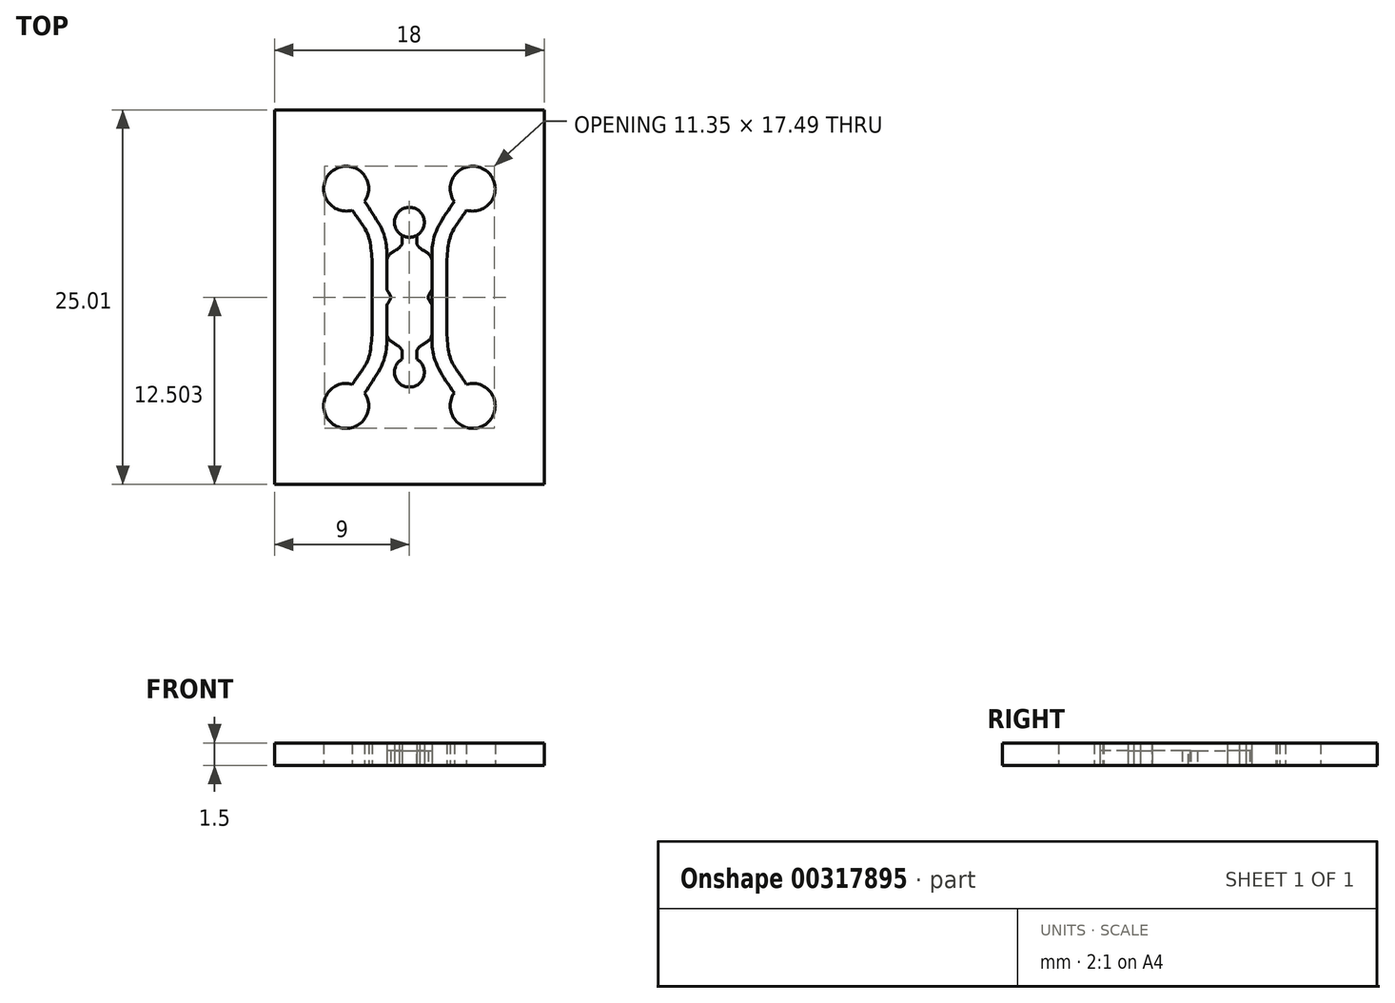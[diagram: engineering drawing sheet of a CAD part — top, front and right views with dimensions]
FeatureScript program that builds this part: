
annotation { "Feature Type Name" : "Feature", "Feature Type Description" : "" }
export const myFeature = defineFeature(function(context is Context, id is Id, definition is map)
    precondition{}
    {
        {
            var Q0;
            Q0=qCreatedBy(makeId("Top.planeOp"),FACE);
            var sketch = newSketch(context, id + "F0", { "sketchPlane" : qUnion([Q0])});
            skPoint(sketch, "E0.1.0.27", {"position": v(-35.15, 26.8) * mm});
            skCircle(sketch, "E1", {"center": v(0, 13.86) * mm, "radius": 50 * mm});
            skLineSegment(sketch, "E2", {"start": v(-12.54, -30.64) * mm, "end": v(-12.54, -12.64) * mm});
            skLineSegment(sketch, "E3", {"start": v(0, 13.86) * mm, "end": v(-50, 13.86) * mm});
            skLineSegment(sketch, "E4", {"start": v(-12.54, -12.64) * mm, "end": v(12.46, -12.64) * mm});
            skLineSegment(sketch, "E5", {"start": v(-12.54, -30.64) * mm, "end": v(12.46, -30.64) * mm});
            skLineSegment(sketch, "E6", {"start": v(12.46, -30.64) * mm, "end": v(12.46, -12.64) * mm});
            skLineSegment(sketch, "E7.left", {"start": v(-27.05, 0.86) * mm, "end": v(-27.05, -1.64) * mm});
            skLineSegment(sketch, "E8", {"start": v(-28.07, -3.26) * mm, "end": v(-28.07, -2.89) * mm});
            skFitSpline(sketch, "E9", {"points": [v(-28.07, -2.89) * mm, v(-28.05, -2.69) * mm, v(-27.87, -2.44) * mm], "startDerivative": vector(0, 0.47) * mm, "endDerivative": vector(0.58, 0.57) * mm});
            skFitSpline(sketch, "E10", {"points": [v(-27.87, -2.44) * mm, v(-27.6, -2.26) * mm, v(-27.23, -2) * mm, v(-27.05, -1.64) * mm], "startDerivative": vector(0.53, 0.49) * mm, "endDerivative": vector(0.1, 0.95) * mm});
            skLineSegment(sketch, "E11", {"start": v(-26.05, 0.86) * mm, "end": v(-26.05, -1.66) * mm});
            skPoint(sketch, "E12.third.point", {"position": v(-24.15, -7.57) * mm});
            skFitSpline(sketch, "E13", {"points": [v(-27.05, -1.64) * mm, v(-27.05, -2.14) * mm, v(-26.8, -3.43) * mm, v(-25.56, -5.53) * mm], "startDerivative": vector(-0.07, -2.14) * mm, "endDerivative": vector(3.18, -4.62) * mm});
            skPoint(sketch, "E14.third.point", {"position": v(-23.83, -5.88) * mm});
            skPoint(sketch, "E15.third.point", {"position": v(-22.85, -6.64) * mm});
            skArc(sketch, "E16", {"start": v(-28.55, -5.14) * mm, "mid": v(-27.58, -4.39) * mm, "end": v(-28.07, -3.26) * mm});
            skArc(sketch, "E17", {"start": v(-25.56, -5.53) * mm, "mid": v(-23.46, -7.6) * mm, "end": v(-24.74, -4.95) * mm});
            skFitSpline(sketch, "E18.MirrorCS", {"points": [v(-29.03, -2.89) * mm, v(-29.05, -2.69) * mm, v(-29.23, -2.44) * mm], "startDerivative": vector(0, 0.47) * mm, "endDerivative": vector(-0.58, 0.57) * mm});
            skLineSegment(sketch, "E19.MirrorCS", {"start": v(-29.03, -3.26) * mm, "end": v(-29.03, -2.89) * mm});
            skFitSpline(sketch, "E20.MirrorCS", {"points": [v(-29.23, -2.44) * mm, v(-29.5, -2.26) * mm, v(-29.87, -2) * mm, v(-30.05, -1.64) * mm], "startDerivative": vector(-0.53, 0.49) * mm, "endDerivative": vector(-0.1, 0.95) * mm});
            skPoint(sketch, "E21.MirrorP", {"position": v(-33.27, -5.88) * mm});
            skPoint(sketch, "E22.MirrorP", {"position": v(-32.95, -7.57) * mm});
            skArc(sketch, "E23.MirrorCS", {"start": v(-28.55, -5.14) * mm, "mid": v(-29.52, -4.39) * mm, "end": v(-29.03, -3.26) * mm});
            skArc(sketch, "E24.MirrorCS", {"start": v(-31.54, -5.53) * mm, "mid": v(-33.64, -7.6) * mm, "end": v(-32.36, -4.95) * mm});
            skLineSegment(sketch, "E25.MirrorCS", {"start": v(-30.05, 0.86) * mm, "end": v(-30.05, -1.64) * mm});
            skLineSegment(sketch, "E26.MirrorCS", {"start": v(-31.05, 0.86) * mm, "end": v(-31.05, -1.66) * mm});
            skFitSpline(sketch, "E27.MirrorCS", {"points": [v(-30.05, -1.64) * mm, v(-30.05, -2.14) * mm, v(-30.3, -3.43) * mm, v(-31.54, -5.53) * mm], "startDerivative": vector(0.07, -2.14) * mm, "endDerivative": vector(-3.18, -4.62) * mm});
            skPoint(sketch, "E28.MirrorP", {"position": v(-34.25, -6.64) * mm});
            skFitSpline(sketch, "E29", {"points": [v(-26.05, -1.66) * mm, v(-25.8, -3.26) * mm, v(-25.24, -4.22) * mm, v(-24.74, -4.95) * mm], "startDerivative": vector(0.34, -4.39) * mm, "endDerivative": vector(1.65, -2.5) * mm});
            skFitSpline(sketch, "E30.MirrorCS", {"points": [v(-31.05, -1.66) * mm, v(-31.3, -3.26) * mm, v(-31.86, -4.22) * mm, v(-32.36, -4.95) * mm], "startDerivative": vector(-0.34, -4.39) * mm, "endDerivative": vector(-1.65, -2.5) * mm});
            skCircle(sketch, "E31", {"center": v(-28.55, -4.14) * mm, "radius": 1 * mm});
            skFitSpline(sketch, "E32.MirrorCS", {"points": [v(-28.07, 4.61) * mm, v(-28.05, 4.41) * mm, v(-27.87, 4.17) * mm], "startDerivative": vector(0, -0.47) * mm, "endDerivative": vector(0.58, -0.57) * mm});
            skFitSpline(sketch, "E33.MirrorCS", {"points": [v(-29.03, 4.61) * mm, v(-29.05, 4.41) * mm, v(-29.23, 4.17) * mm], "startDerivative": vector(0, -0.47) * mm, "endDerivative": vector(-0.58, -0.57) * mm});
            skFitSpline(sketch, "E34.MirrorCS", {"points": [v(-27.87, 4.17) * mm, v(-27.6, 3.98) * mm, v(-27.23, 3.72) * mm, v(-27.05, 3.36) * mm], "startDerivative": vector(0.53, -0.49) * mm, "endDerivative": vector(0.1, -0.95) * mm});
            skFitSpline(sketch, "E35.MirrorCS", {"points": [v(-29.23, 4.17) * mm, v(-29.5, 3.98) * mm, v(-29.87, 3.72) * mm, v(-30.05, 3.36) * mm], "startDerivative": vector(-0.53, -0.49) * mm, "endDerivative": vector(-0.1, -0.95) * mm});
            skLineSegment(sketch, "E36.MirrorCS", {"start": v(-28.07, 4.99) * mm, "end": v(-28.07, 4.61) * mm});
            skLineSegment(sketch, "E37.MirrorCS", {"start": v(-29.03, 4.99) * mm, "end": v(-29.03, 4.61) * mm});
            skArc(sketch, "E38.MirrorCS", {"start": v(-28.55, 6.86) * mm, "mid": v(-27.58, 6.11) * mm, "end": v(-28.07, 4.99) * mm});
            skPoint(sketch, "E39.MirrorP", {"position": v(-32.95, 9.3) * mm});
            skFitSpline(sketch, "E40.MirrorCS", {"points": [v(-31.05, 3.4) * mm, v(-31.3, 4.99) * mm, v(-31.86, 5.94) * mm, v(-32.36, 6.67) * mm], "startDerivative": vector(-0.34, 4.39) * mm, "endDerivative": vector(-1.65, 2.5) * mm});
            skLineSegment(sketch, "E41.MirrorCS", {"start": v(-26.05, 0.86) * mm, "end": v(-26.05, 3.4) * mm});
            skLineSegment(sketch, "E42.MirrorCS", {"start": v(-27.05, 0.86) * mm, "end": v(-27.05, 3.36) * mm});
            skPoint(sketch, "E43.MirrorP", {"position": v(-22.85, 8.36) * mm});
            skFitSpline(sketch, "E44.MirrorCS", {"points": [v(-30.05, 3.36) * mm, v(-30.05, 3.86) * mm, v(-30.3, 5.15) * mm, v(-31.54, 7.25) * mm], "startDerivative": vector(0.07, 2.14) * mm, "endDerivative": vector(-3.18, 4.62) * mm});
            skPoint(sketch, "E45.MirrorP", {"position": v(-24.15, 9.3) * mm});
            skLineSegment(sketch, "E46.MirrorCS", {"start": v(-31.05, 0.86) * mm, "end": v(-31.05, 3.4) * mm});
            skLineSegment(sketch, "E47.MirrorCS", {"start": v(-30.05, 0.86) * mm, "end": v(-30.05, 3.36) * mm});
            skFitSpline(sketch, "E48.MirrorCS", {"points": [v(-27.05, 3.36) * mm, v(-27.05, 3.86) * mm, v(-26.8, 5.15) * mm, v(-25.56, 7.25) * mm], "startDerivative": vector(-0.07, 2.14) * mm, "endDerivative": vector(3.18, 4.62) * mm});
            skCircle(sketch, "E49.MirrorC", {"center": v(-28.55, 5.86) * mm, "radius": 1 * mm});
            skPoint(sketch, "E50.MirrorP", {"position": v(-34.25, 8.36) * mm});
            skFitSpline(sketch, "E51.MirrorCS", {"points": [v(-26.05, 3.4) * mm, v(-25.8, 4.99) * mm, v(-25.24, 5.94) * mm, v(-24.74, 6.67) * mm], "startDerivative": vector(0.34, 4.39) * mm, "endDerivative": vector(1.65, 2.5) * mm});
            skArc(sketch, "E52.MirrorCS", {"start": v(-28.55, 6.86) * mm, "mid": v(-29.52, 6.11) * mm, "end": v(-29.03, 4.99) * mm});
            skArc(sketch, "E53.MirrorCS", {"start": v(-25.56, 7.25) * mm, "mid": v(-23.46, 9.34) * mm, "end": v(-24.74, 6.67) * mm});
            skPoint(sketch, "E54.MirrorP", {"position": v(-23.83, 7.6) * mm});
            skArc(sketch, "E55.MirrorCS", {"start": v(-31.54, 7.25) * mm, "mid": v(-33.64, 9.34) * mm, "end": v(-32.36, 6.67) * mm});
            skPoint(sketch, "E56.MirrorP", {"position": v(-33.27, 7.6) * mm});
            skFitSpline(sketch, "E57", {"points": [v(-29.8, 0.86) * mm, v(-29.81, 0.79) * mm, v(-30.05, 0.36) * mm], "startDerivative": vector(0, -0.22) * mm, "endDerivative": vector(-0.44, -0.71) * mm});
            skArc(sketch, "E58", {"start": v(-29.81, 0.79) * mm, "mid": v(-29.8, 0.83) * mm, "end": v(-29.8, 0.86) * mm});
            skFitSpline(sketch, "E59.MirrorCS", {"points": [v(-29.8, 0.86) * mm, v(-29.81, 0.94) * mm, v(-30.05, 1.36) * mm], "startDerivative": vector(0, 0.22) * mm, "endDerivative": vector(-0.44, 0.71) * mm});
            skArc(sketch, "E60.MirrorCS", {"start": v(-29.81, 0.94) * mm, "mid": v(-29.8, 0.9) * mm, "end": v(-29.8, 0.86) * mm});
            skArc(sketch, "E61.MirrorCS", {"start": v(-27.29, 0.79) * mm, "mid": v(-27.3, 0.83) * mm, "end": v(-27.3, 0.86) * mm});
            skArc(sketch, "E62.MirrorCS", {"start": v(-27.29, 0.94) * mm, "mid": v(-27.3, 0.9) * mm, "end": v(-27.3, 0.86) * mm});
            skFitSpline(sketch, "E63.MirrorCS", {"points": [v(-27.3, 0.86) * mm, v(-27.29, 0.79) * mm, v(-27.05, 0.36) * mm], "startDerivative": vector(0, -0.22) * mm, "endDerivative": vector(0.44, -0.71) * mm});
            skFitSpline(sketch, "E64.MirrorCS", {"points": [v(-27.3, 0.86) * mm, v(-27.29, 0.94) * mm, v(-27.05, 1.36) * mm], "startDerivative": vector(0, 0.22) * mm, "endDerivative": vector(0.44, 0.71) * mm});
            skCircle(sketch, "E65.MirrorC", {"center": v(0, 11.64) * mm, "radius": 1 * mm});
            skLineSegment(sketch, "E66.right", {"start": v(-37.55, -11.64) * mm, "end": v(-37.55, 13.37) * mm});
            skLineSegment(sketch, "E67.bottom", {"start": v(-19.55, 13.37) * mm, "end": v(-37.55, 13.37) * mm});
            skLineSegment(sketch, "E67.top", {"start": v(-19.55, -11.64) * mm, "end": v(-37.55, -11.64) * mm});
            skLineSegment(sketch, "E67.left", {"start": v(-19.55, 13.37) * mm, "end": v(-19.55, -11.64) * mm});
            skLineSegment(sketch, "E67.right", {"start": v(-37.55, 13.37) * mm, "end": v(-37.55, -11.64) * mm});
            skArc(sketch, "E68.MirrorCS", {"start": v(-0.06, -22.85) * mm, "mid": v(-0.02, -22.84) * mm, "end": v(0.01, -22.83) * mm});
            skFitSpline(sketch, "E69.MirrorCS", {"points": [v(0.01, -22.83) * mm, v(-0.06, -22.85) * mm, v(-0.49, -23.08) * mm], "startDerivative": vector(-0.22, 0) * mm, "endDerivative": vector(-0.71, -0.44) * mm});
            skArc(sketch, "E70.MirrorCS", {"start": v(0.09, -22.85) * mm, "mid": v(0.05, -22.84) * mm, "end": v(0.01, -22.83) * mm});
            skFitSpline(sketch, "E71.MirrorCS", {"points": [v(0.01, -22.83) * mm, v(0.09, -22.85) * mm, v(0.51, -23.08) * mm], "startDerivative": vector(0.22, 0) * mm, "endDerivative": vector(0.71, -0.44) * mm});
            skArc(sketch, "E72.MirrorCS", {"start": v(-0.06, -20.32) * mm, "mid": v(-0.02, -20.33) * mm, "end": v(0.01, -20.33) * mm});
            skFitSpline(sketch, "E73.MirrorCS", {"points": [v(0.01, -20.33) * mm, v(0.09, -20.32) * mm, v(0.51, -20.08) * mm], "startDerivative": vector(0.22, 0) * mm, "endDerivative": vector(0.71, 0.44) * mm});
            skFitSpline(sketch, "E74.MirrorCS", {"points": [v(0.01, -20.33) * mm, v(-0.06, -20.32) * mm, v(-0.49, -20.08) * mm], "startDerivative": vector(-0.22, 0) * mm, "endDerivative": vector(-0.71, 0.44) * mm});
            skArc(sketch, "E75.MirrorCS", {"start": v(0.09, -20.32) * mm, "mid": v(0.05, -20.33) * mm, "end": v(0.01, -20.33) * mm});
            skFitSpline(sketch, "E76.MirrorCS", {"points": [v(3.32, -22.26) * mm, v(3.13, -22.53) * mm, v(2.87, -22.9) * mm, v(2.51, -23.08) * mm], "startDerivative": vector(-0.49, -0.53) * mm, "endDerivative": vector(-0.95, -0.1) * mm});
            skFitSpline(sketch, "E77.MirrorCS", {"points": [v(3.76, -22.07) * mm, v(3.56, -22.08) * mm, v(3.32, -22.26) * mm], "startDerivative": vector(-0.47, 0) * mm, "endDerivative": vector(-0.57, -0.58) * mm});
            skLineSegment(sketch, "E78.MirrorCS", {"start": v(4.14, -22.07) * mm, "end": v(3.76, -22.07) * mm});
            skFitSpline(sketch, "E79.MirrorCS", {"points": [v(3.32, -20.9) * mm, v(3.13, -20.63) * mm, v(2.87, -20.26) * mm, v(2.51, -20.08) * mm], "startDerivative": vector(-0.49, 0.53) * mm, "endDerivative": vector(-0.95, 0.1) * mm});
            skFitSpline(sketch, "E80.MirrorCS", {"points": [v(3.76, -21.1) * mm, v(3.56, -21.08) * mm, v(3.32, -20.9) * mm], "startDerivative": vector(-0.47, 0) * mm, "endDerivative": vector(-0.57, 0.58) * mm});
            skLineSegment(sketch, "E81.MirrorCS", {"start": v(4.14, -21.1) * mm, "end": v(3.76, -21.1) * mm});
            skFitSpline(sketch, "E82.MirrorCS", {"points": [v(-3.29, -22.26) * mm, v(-3.1, -22.53) * mm, v(-2.84, -22.9) * mm, v(-2.49, -23.08) * mm], "startDerivative": vector(0.49, -0.53) * mm, "endDerivative": vector(0.95, -0.1) * mm});
            skFitSpline(sketch, "E83.MirrorCS", {"points": [v(-3.29, -20.9) * mm, v(-3.1, -20.63) * mm, v(-2.84, -20.26) * mm, v(-2.49, -20.08) * mm], "startDerivative": vector(0.49, 0.53) * mm, "endDerivative": vector(0.95, 0.1) * mm});
            skLineSegment(sketch, "E84.MirrorCS", {"start": v(-4.11, -22.07) * mm, "end": v(-3.74, -22.07) * mm});
            skFitSpline(sketch, "E85.MirrorCS", {"points": [v(-3.74, -21.1) * mm, v(-3.54, -21.08) * mm, v(-3.29, -20.9) * mm], "startDerivative": vector(0.47, 0) * mm, "endDerivative": vector(0.57, 0.58) * mm});
            skFitSpline(sketch, "E86.MirrorCS", {"points": [v(-3.74, -22.07) * mm, v(-3.54, -22.08) * mm, v(-3.29, -22.26) * mm], "startDerivative": vector(0.47, 0) * mm, "endDerivative": vector(0.57, -0.58) * mm});
            skLineSegment(sketch, "E87.MirrorCS", {"start": v(-4.11, -21.1) * mm, "end": v(-3.74, -21.1) * mm});
            skLineSegment(sketch, "E88.MirrorCS", {"start": v(0.01, -23.08) * mm, "end": v(-2.49, -23.08) * mm});
            skLineSegment(sketch, "E89.MirrorCS", {"start": v(0.01, -20.08) * mm, "end": v(2.51, -20.08) * mm});
            skLineSegment(sketch, "E90.MirrorCS", {"start": v(0.01, -19.08) * mm, "end": v(-2.51, -19.08) * mm});
            skLineSegment(sketch, "E91.MirrorCS", {"start": v(0.01, -19.08) * mm, "end": v(2.54, -19.08) * mm});
            skFitSpline(sketch, "E92.MirrorCS", {"points": [v(2.54, -24.08) * mm, v(4.14, -24.34) * mm, v(5.1, -24.9) * mm, v(5.82, -25.4) * mm], "startDerivative": vector(4.39, -0.34) * mm, "endDerivative": vector(2.5, -1.65) * mm});
            skFitSpline(sketch, "E93.MirrorCS", {"points": [v(2.54, -19.08) * mm, v(4.14, -18.83) * mm, v(5.1, -18.27) * mm, v(5.82, -17.78) * mm], "startDerivative": vector(4.39, 0.34) * mm, "endDerivative": vector(2.5, 1.65) * mm});
            skLineSegment(sketch, "E94.MirrorCS", {"start": v(0.01, -20.08) * mm, "end": v(-2.49, -20.08) * mm});
            skFitSpline(sketch, "E95.MirrorCS", {"points": [v(-2.51, -24.08) * mm, v(-4.1, -24.34) * mm, v(-5.07, -24.9) * mm, v(-5.8, -25.4) * mm], "startDerivative": vector(-4.39, -0.34) * mm, "endDerivative": vector(-2.5, -1.65) * mm});
            skLineSegment(sketch, "E96.MirrorCS", {"start": v(0.01, -23.08) * mm, "end": v(2.51, -23.08) * mm});
            skLineSegment(sketch, "E97.MirrorCS", {"start": v(0.01, -24.08) * mm, "end": v(2.54, -24.08) * mm});
            skLineSegment(sketch, "E98.MirrorCS", {"start": v(0.01, -24.08) * mm, "end": v(-2.51, -24.08) * mm});
            skArc(sketch, "E99.MirrorCS", {"start": v(-5.99, -21.58) * mm, "mid": v(-5.24, -20.62) * mm, "end": v(-4.11, -21.1) * mm});
            skFitSpline(sketch, "E100.MirrorCS", {"points": [v(2.51, -23.08) * mm, v(3.01, -23.08) * mm, v(4.3, -23.33) * mm, v(6.4, -24.58) * mm], "startDerivative": vector(2.14, 0.07) * mm, "endDerivative": vector(4.62, -3.18) * mm});
            skFitSpline(sketch, "E101.MirrorCS", {"points": [v(-2.49, -20.08) * mm, v(-2.99, -20.08) * mm, v(-4.28, -19.84) * mm, v(-6.38, -18.59) * mm], "startDerivative": vector(-2.14, -0.07) * mm, "endDerivative": vector(-4.62, 3.18) * mm});
            skArc(sketch, "E102.MirrorCS", {"start": v(6.01, -21.58) * mm, "mid": v(5.26, -20.62) * mm, "end": v(4.14, -21.1) * mm});
            skCircle(sketch, "E103.MirrorC", {"center": v(-4.99, -21.58) * mm, "radius": 1 * mm});
            skFitSpline(sketch, "E104.MirrorCS", {"points": [v(-2.51, -19.08) * mm, v(-4.1, -18.83) * mm, v(-5.07, -18.27) * mm, v(-5.8, -17.78) * mm], "startDerivative": vector(-4.39, 0.34) * mm, "endDerivative": vector(-2.5, 1.65) * mm});
            skFitSpline(sketch, "E105.MirrorCS", {"points": [v(2.51, -20.08) * mm, v(3.01, -20.08) * mm, v(4.3, -19.84) * mm, v(6.4, -18.59) * mm], "startDerivative": vector(2.14, -0.07) * mm, "endDerivative": vector(4.62, 3.18) * mm});
            skCircle(sketch, "E106.MirrorC", {"center": v(5.01, -21.58) * mm, "radius": 1 * mm});
            skFitSpline(sketch, "E107.MirrorCS", {"points": [v(-2.49, -23.08) * mm, v(-2.99, -23.08) * mm, v(-4.28, -23.33) * mm, v(-6.38, -24.58) * mm], "startDerivative": vector(-2.14, 0.07) * mm, "endDerivative": vector(-4.62, -3.18) * mm});
            skPoint(sketch, "E108.MirrorP", {"position": v(7.51, -15.88) * mm});
            skPoint(sketch, "E109.MirrorP", {"position": v(8.44, -17.18) * mm});
            skArc(sketch, "E110.MirrorCS", {"start": v(6.4, -24.58) * mm, "mid": v(8.49, -26.68) * mm, "end": v(5.82, -25.4) * mm});
            skPoint(sketch, "E111.MirrorP", {"position": v(7.51, -27.28) * mm});
            skArc(sketch, "E112.MirrorCS", {"start": v(-6.38, -24.58) * mm, "mid": v(-8.46, -26.68) * mm, "end": v(-5.8, -25.4) * mm});
            skArc(sketch, "E113.MirrorCS", {"start": v(-5.99, -21.58) * mm, "mid": v(-5.24, -22.55) * mm, "end": v(-4.11, -22.07) * mm});
            skArc(sketch, "E114.MirrorCS", {"start": v(6.4, -18.59) * mm, "mid": v(8.49, -16.5) * mm, "end": v(5.82, -17.78) * mm});
            skArc(sketch, "E115.MirrorCS", {"start": v(6.01, -21.58) * mm, "mid": v(5.26, -22.55) * mm, "end": v(4.14, -22.07) * mm});
            skPoint(sketch, "E116.MirrorP", {"position": v(-7.49, -27.28) * mm});
            skPoint(sketch, "E117.MirrorP", {"position": v(-8.42, -17.18) * mm});
            skPoint(sketch, "E118.MirrorP", {"position": v(-6.73, -26.3) * mm});
            skPoint(sketch, "E119.MirrorP", {"position": v(6.76, -26.3) * mm});
            skPoint(sketch, "E120.MirrorP", {"position": v(-7.49, -15.88) * mm});
            skPoint(sketch, "E121.MirrorP", {"position": v(-6.73, -16.86) * mm});
            skPoint(sketch, "E122.MirrorP", {"position": v(-8.42, -25.99) * mm});
            skPoint(sketch, "E123.MirrorP", {"position": v(8.44, -25.99) * mm});
            skArc(sketch, "E124.MirrorCS", {"start": v(-6.38, -18.59) * mm, "mid": v(-8.46, -16.5) * mm, "end": v(-5.8, -17.78) * mm});
            skPoint(sketch, "E125.MirrorP", {"position": v(6.76, -16.86) * mm});
            skFitSpline(sketch, "E126.MirrorCS", {"points": [v(0.01, -20.33) * mm, v(0.09, -20.32) * mm, v(0.51, -20.08) * mm], "startDerivative": vector(0.22, 0) * mm, "endDerivative": vector(0.71, 0.44) * mm});
            skFitSpline(sketch, "E127.MirrorCS", {"points": [v(0.01, -20.33) * mm, v(-0.06, -20.32) * mm, v(-0.49, -20.08) * mm], "startDerivative": vector(-0.22, 0) * mm, "endDerivative": vector(-0.71, 0.44) * mm});
            skFitSpline(sketch, "E128.MirrorCS", {"points": [v(0.01, -22.83) * mm, v(0.09, -22.85) * mm, v(0.51, -23.08) * mm], "startDerivative": vector(0.22, 0) * mm, "endDerivative": vector(0.71, -0.44) * mm});
            skFitSpline(sketch, "E129.MirrorCS", {"points": [v(0.01, -22.83) * mm, v(-0.06, -22.85) * mm, v(-0.49, -23.08) * mm], "startDerivative": vector(-0.22, 0) * mm, "endDerivative": vector(-0.71, -0.44) * mm});
            skFitSpline(sketch, "E130.MirrorCS", {"points": [v(-3.29, -22.26) * mm, v(-3.1, -22.53) * mm, v(-2.84, -22.9) * mm, v(-2.49, -23.08) * mm], "startDerivative": vector(0.49, -0.53) * mm, "endDerivative": vector(0.95, -0.1) * mm});
            skFitSpline(sketch, "E131.MirrorCS", {"points": [v(-3.29, -20.9) * mm, v(-3.1, -20.63) * mm, v(-2.84, -20.26) * mm, v(-2.49, -20.08) * mm], "startDerivative": vector(0.49, 0.53) * mm, "endDerivative": vector(0.95, 0.1) * mm});
            skFitSpline(sketch, "E132.MirrorCS", {"points": [v(3.32, -20.9) * mm, v(3.13, -20.63) * mm, v(2.87, -20.26) * mm, v(2.51, -20.08) * mm], "startDerivative": vector(-0.49, 0.53) * mm, "endDerivative": vector(-0.95, 0.1) * mm});
            skFitSpline(sketch, "E133.MirrorCS", {"points": [v(-3.74, -21.1) * mm, v(-3.54, -21.08) * mm, v(-3.29, -20.9) * mm], "startDerivative": vector(0.47, 0) * mm, "endDerivative": vector(0.57, 0.58) * mm});
            skFitSpline(sketch, "E134.MirrorCS", {"points": [v(3.32, -22.26) * mm, v(3.13, -22.53) * mm, v(2.87, -22.9) * mm, v(2.51, -23.08) * mm], "startDerivative": vector(-0.49, -0.53) * mm, "endDerivative": vector(-0.95, -0.1) * mm});
            skFitSpline(sketch, "E135.MirrorCS", {"points": [v(3.76, -21.1) * mm, v(3.56, -21.08) * mm, v(3.32, -20.9) * mm], "startDerivative": vector(-0.47, 0) * mm, "endDerivative": vector(-0.57, 0.58) * mm});
            skFitSpline(sketch, "E136.MirrorCS", {"points": [v(-2.51, -19.08) * mm, v(-4.1, -18.83) * mm, v(-5.07, -18.27) * mm, v(-5.8, -17.78) * mm], "startDerivative": vector(-4.39, 0.34) * mm, "endDerivative": vector(-2.5, 1.65) * mm});
            skFitSpline(sketch, "E137.MirrorCS", {"points": [v(-2.51, -24.08) * mm, v(-4.1, -24.34) * mm, v(-5.07, -24.9) * mm, v(-5.8, -25.4) * mm], "startDerivative": vector(-4.39, -0.34) * mm, "endDerivative": vector(-2.5, -1.65) * mm});
            skFitSpline(sketch, "E138.MirrorCS", {"points": [v(-2.49, -23.08) * mm, v(-2.99, -23.08) * mm, v(-4.28, -23.33) * mm, v(-6.38, -24.58) * mm], "startDerivative": vector(-2.14, 0.07) * mm, "endDerivative": vector(-4.62, -3.18) * mm});
            skFitSpline(sketch, "E139.MirrorCS", {"points": [v(-2.49, -20.08) * mm, v(-2.99, -20.08) * mm, v(-4.28, -19.84) * mm, v(-6.38, -18.59) * mm], "startDerivative": vector(-2.14, -0.07) * mm, "endDerivative": vector(-4.62, 3.18) * mm});
            skArc(sketch, "E140.MirrorCS", {"start": v(-0.06, 48.05) * mm, "mid": v(-0.02, 48.06) * mm, "end": v(0.01, 48.06) * mm});
            skArc(sketch, "E141.MirrorCS", {"start": v(0.09, 48.05) * mm, "mid": v(0.05, 48.06) * mm, "end": v(0.01, 48.06) * mm});
            skLineSegment(sketch, "E142.MirrorCS", {"start": v(0.01, 46.81) * mm, "end": v(-2.51, 46.81) * mm});
            skLineSegment(sketch, "E143.MirrorCS", {"start": v(0.01, 47.81) * mm, "end": v(-2.49, 47.81) * mm});
            skFitSpline(sketch, "E144.MirrorCS", {"points": [v(0.01, 48.06) * mm, v(0.09, 48.05) * mm, v(0.51, 47.81) * mm], "startDerivative": vector(0.22, 0) * mm, "endDerivative": vector(0.71, -0.44) * mm});
            skFitSpline(sketch, "E145.MirrorCS", {"points": [v(0.01, 48.06) * mm, v(-0.06, 48.05) * mm, v(-0.49, 47.81) * mm], "startDerivative": vector(-0.22, 0) * mm, "endDerivative": vector(-0.71, -0.44) * mm});
            skFitSpline(sketch, "E146.MirrorCS", {"points": [v(0.01, 48.06) * mm, v(-0.06, 48.05) * mm, v(-0.49, 47.81) * mm], "startDerivative": vector(-0.22, 0) * mm, "endDerivative": vector(-0.71, -0.44) * mm});
            skFitSpline(sketch, "E147.MirrorCS", {"points": [v(0.01, 48.06) * mm, v(0.09, 48.05) * mm, v(0.51, 47.81) * mm], "startDerivative": vector(0.22, 0) * mm, "endDerivative": vector(0.71, -0.44) * mm});
            skArc(sketch, "E148.MirrorCS", {"start": v(-0.06, 50.57) * mm, "mid": v(-0.02, 50.57) * mm, "end": v(0.01, 50.56) * mm});
            skArc(sketch, "E149.MirrorCS", {"start": v(0.09, 50.57) * mm, "mid": v(0.05, 50.57) * mm, "end": v(0.01, 50.56) * mm});
            skFitSpline(sketch, "E150.MirrorCS", {"points": [v(0.01, 50.56) * mm, v(0.09, 50.57) * mm, v(0.51, 50.81) * mm], "startDerivative": vector(0.22, 0) * mm, "endDerivative": vector(0.71, 0.44) * mm});
            skLineSegment(sketch, "E151.MirrorCS", {"start": v(0.01, 50.81) * mm, "end": v(-2.49, 50.81) * mm});
            skFitSpline(sketch, "E152.MirrorCS", {"points": [v(0.01, 50.56) * mm, v(-0.06, 50.57) * mm, v(-0.49, 50.81) * mm], "startDerivative": vector(-0.22, 0) * mm, "endDerivative": vector(-0.71, 0.44) * mm});
            skLineSegment(sketch, "E153.MirrorCS", {"start": v(0.01, 51.81) * mm, "end": v(-2.51, 51.81) * mm});
            skFitSpline(sketch, "E154.MirrorCS", {"points": [v(0.01, 50.56) * mm, v(0.09, 50.57) * mm, v(0.51, 50.81) * mm], "startDerivative": vector(0.22, 0) * mm, "endDerivative": vector(0.71, 0.44) * mm});
            skFitSpline(sketch, "E155.MirrorCS", {"points": [v(0.01, 50.56) * mm, v(-0.06, 50.57) * mm, v(-0.49, 50.81) * mm], "startDerivative": vector(-0.22, 0) * mm, "endDerivative": vector(-0.71, 0.44) * mm});
            skLineSegment(sketch, "E156.MirrorCS", {"start": v(-4.11, 49.8) * mm, "end": v(-3.74, 49.8) * mm});
            skFitSpline(sketch, "E157.MirrorCS", {"points": [v(-3.29, 48.63) * mm, v(-3.1, 48.36) * mm, v(-2.84, 48) * mm, v(-2.49, 47.81) * mm], "startDerivative": vector(0.49, -0.53) * mm, "endDerivative": vector(0.95, -0.1) * mm});
            skLineSegment(sketch, "E158.MirrorCS", {"start": v(-4.11, 48.83) * mm, "end": v(-3.74, 48.83) * mm});
            skFitSpline(sketch, "E159.MirrorCS", {"points": [v(-3.74, 48.83) * mm, v(-3.54, 48.81) * mm, v(-3.29, 48.63) * mm], "startDerivative": vector(0.47, 0) * mm, "endDerivative": vector(0.57, -0.58) * mm});
            skLineSegment(sketch, "E160.MirrorCS", {"start": v(0.01, 47.81) * mm, "end": v(2.51, 47.81) * mm});
            skFitSpline(sketch, "E161.MirrorCS", {"points": [v(-3.29, 50) * mm, v(-3.1, 50.26) * mm, v(-2.84, 50.63) * mm, v(-2.49, 50.81) * mm], "startDerivative": vector(0.49, 0.53) * mm, "endDerivative": vector(0.95, 0.1) * mm});
            skFitSpline(sketch, "E162.MirrorCS", {"points": [v(3.76, 49.8) * mm, v(3.56, 49.81) * mm, v(3.32, 50) * mm], "startDerivative": vector(-0.47, 0) * mm, "endDerivative": vector(-0.57, 0.58) * mm});
            skFitSpline(sketch, "E163.MirrorCS", {"points": [v(-3.74, 49.8) * mm, v(-3.54, 49.81) * mm, v(-3.29, 50) * mm], "startDerivative": vector(0.47, 0) * mm, "endDerivative": vector(0.57, 0.58) * mm});
            skFitSpline(sketch, "E164.MirrorCS", {"points": [v(-3.74, 48.83) * mm, v(-3.54, 48.81) * mm, v(-3.29, 48.63) * mm], "startDerivative": vector(0.47, 0) * mm, "endDerivative": vector(0.57, -0.58) * mm});
            skLineSegment(sketch, "E165.MirrorCS", {"start": v(4.14, 49.8) * mm, "end": v(3.76, 49.8) * mm});
            skFitSpline(sketch, "E166.MirrorCS", {"points": [v(3.32, 48.63) * mm, v(3.13, 48.36) * mm, v(2.87, 48) * mm, v(2.51, 47.81) * mm], "startDerivative": vector(-0.49, -0.53) * mm, "endDerivative": vector(-0.95, -0.1) * mm});
            skFitSpline(sketch, "E167.MirrorCS", {"points": [v(3.32, 50) * mm, v(3.13, 50.26) * mm, v(2.87, 50.63) * mm, v(2.51, 50.81) * mm], "startDerivative": vector(-0.49, 0.53) * mm, "endDerivative": vector(-0.95, 0.1) * mm});
            skFitSpline(sketch, "E168.MirrorCS", {"points": [v(-3.29, 48.63) * mm, v(-3.1, 48.36) * mm, v(-2.84, 48) * mm, v(-2.49, 47.81) * mm], "startDerivative": vector(0.49, -0.53) * mm, "endDerivative": vector(0.95, -0.1) * mm});
            skFitSpline(sketch, "E169.MirrorCS", {"points": [v(-3.29, 50) * mm, v(-3.1, 50.26) * mm, v(-2.84, 50.63) * mm, v(-2.49, 50.81) * mm], "startDerivative": vector(0.49, 0.53) * mm, "endDerivative": vector(0.95, 0.1) * mm});
            skFitSpline(sketch, "E170.MirrorCS", {"points": [v(-3.74, 49.8) * mm, v(-3.54, 49.81) * mm, v(-3.29, 50) * mm], "startDerivative": vector(0.47, 0) * mm, "endDerivative": vector(0.57, 0.58) * mm});
            skLineSegment(sketch, "E171.MirrorCS", {"start": v(4.14, 48.83) * mm, "end": v(3.76, 48.83) * mm});
            skLineSegment(sketch, "E172.MirrorCS", {"start": v(0.01, 46.81) * mm, "end": v(2.54, 46.81) * mm});
            skFitSpline(sketch, "E173.MirrorCS", {"points": [v(3.76, 48.83) * mm, v(3.56, 48.81) * mm, v(3.32, 48.63) * mm], "startDerivative": vector(-0.47, 0) * mm, "endDerivative": vector(-0.57, -0.58) * mm});
            skFitSpline(sketch, "E174.MirrorCS", {"points": [v(3.32, 50) * mm, v(3.13, 50.26) * mm, v(2.87, 50.63) * mm, v(2.51, 50.81) * mm], "startDerivative": vector(-0.49, 0.53) * mm, "endDerivative": vector(-0.95, 0.1) * mm});
            skFitSpline(sketch, "E175.MirrorCS", {"points": [v(3.32, 48.63) * mm, v(3.13, 48.36) * mm, v(2.87, 48) * mm, v(2.51, 47.81) * mm], "startDerivative": vector(-0.49, -0.53) * mm, "endDerivative": vector(-0.95, -0.1) * mm});
            skFitSpline(sketch, "E176.MirrorCS", {"points": [v(3.76, 48.83) * mm, v(3.56, 48.81) * mm, v(3.32, 48.63) * mm], "startDerivative": vector(-0.47, 0) * mm, "endDerivative": vector(-0.57, -0.58) * mm});
            skLineSegment(sketch, "E177.MirrorCS", {"start": v(0.01, 50.81) * mm, "end": v(2.51, 50.81) * mm});
            skLineSegment(sketch, "E178.MirrorCS", {"start": v(0.01, 51.81) * mm, "end": v(2.54, 51.81) * mm});
            skArc(sketch, "E179.MirrorCS", {"start": v(-5.99, 49.31) * mm, "mid": v(-5.24, 48.35) * mm, "end": v(-4.11, 48.83) * mm});
            skArc(sketch, "E180.MirrorCS", {"start": v(6.01, 49.31) * mm, "mid": v(5.26, 48.35) * mm, "end": v(4.14, 48.83) * mm});
            skCircle(sketch, "E181.MirrorC", {"center": v(5.01, 49.31) * mm, "radius": 1 * mm});
            skCircle(sketch, "E182.MirrorC", {"center": v(-4.99, 49.31) * mm, "radius": 1 * mm});
            skArc(sketch, "E183.MirrorCS", {"start": v(-5.99, 49.31) * mm, "mid": v(-5.24, 50.28) * mm, "end": v(-4.11, 49.8) * mm});
            skFitSpline(sketch, "E184.MirrorCS", {"points": [v(2.51, 47.81) * mm, v(3.01, 47.81) * mm, v(4.3, 47.57) * mm, v(6.4, 46.32) * mm], "startDerivative": vector(2.14, 0.07) * mm, "endDerivative": vector(4.62, -3.18) * mm});
            skFitSpline(sketch, "E185.MirrorCS", {"points": [v(2.54, 46.81) * mm, v(4.14, 46.56) * mm, v(5.1, 46) * mm, v(5.82, 45.5) * mm], "startDerivative": vector(4.39, -0.34) * mm, "endDerivative": vector(2.5, -1.65) * mm});
            skFitSpline(sketch, "E186.MirrorCS", {"points": [v(2.51, 50.81) * mm, v(3.01, 50.81) * mm, v(4.3, 51.06) * mm, v(6.4, 52.3) * mm], "startDerivative": vector(2.14, -0.07) * mm, "endDerivative": vector(4.62, 3.18) * mm});
            skArc(sketch, "E187.MirrorCS", {"start": v(6.01, 49.31) * mm, "mid": v(5.26, 50.28) * mm, "end": v(4.14, 49.8) * mm});
            skFitSpline(sketch, "E188.MirrorCS", {"points": [v(2.51, 47.81) * mm, v(3.01, 47.81) * mm, v(4.3, 47.57) * mm, v(6.4, 46.32) * mm], "startDerivative": vector(2.14, 0.07) * mm, "endDerivative": vector(4.62, -3.18) * mm});
            skFitSpline(sketch, "E189.MirrorCS", {"points": [v(2.54, 46.81) * mm, v(4.14, 46.56) * mm, v(5.1, 46) * mm, v(5.82, 45.5) * mm], "startDerivative": vector(4.39, -0.34) * mm, "endDerivative": vector(2.5, -1.65) * mm});
            skFitSpline(sketch, "E190.MirrorCS", {"points": [v(-2.49, 50.81) * mm, v(-2.99, 50.81) * mm, v(-4.28, 51.06) * mm, v(-6.38, 52.3) * mm], "startDerivative": vector(-2.14, -0.07) * mm, "endDerivative": vector(-4.62, 3.18) * mm});
            skFitSpline(sketch, "E191.MirrorCS", {"points": [v(-2.51, 46.81) * mm, v(-4.1, 46.56) * mm, v(-5.07, 46) * mm, v(-5.8, 45.5) * mm], "startDerivative": vector(-4.39, -0.34) * mm, "endDerivative": vector(-2.5, -1.65) * mm});
            skFitSpline(sketch, "E192.MirrorCS", {"points": [v(-2.49, 47.81) * mm, v(-2.99, 47.81) * mm, v(-4.28, 47.57) * mm, v(-6.38, 46.32) * mm], "startDerivative": vector(-2.14, 0.07) * mm, "endDerivative": vector(-4.62, -3.18) * mm});
            skFitSpline(sketch, "E193.MirrorCS", {"points": [v(2.54, 51.81) * mm, v(4.14, 52.07) * mm, v(5.1, 52.62) * mm, v(5.82, 53.12) * mm], "startDerivative": vector(4.39, 0.34) * mm, "endDerivative": vector(2.5, 1.65) * mm});
            skFitSpline(sketch, "E194.MirrorCS", {"points": [v(-2.49, 47.81) * mm, v(-2.99, 47.81) * mm, v(-4.28, 47.57) * mm, v(-6.38, 46.32) * mm], "startDerivative": vector(-2.14, 0.07) * mm, "endDerivative": vector(-4.62, -3.18) * mm});
            skFitSpline(sketch, "E195.MirrorCS", {"points": [v(-2.51, 46.81) * mm, v(-4.1, 46.56) * mm, v(-5.07, 46) * mm, v(-5.8, 45.5) * mm], "startDerivative": vector(-4.39, -0.34) * mm, "endDerivative": vector(-2.5, -1.65) * mm});
            skFitSpline(sketch, "E196.MirrorCS", {"points": [v(-2.49, 50.81) * mm, v(-2.99, 50.81) * mm, v(-4.28, 51.06) * mm, v(-6.38, 52.3) * mm], "startDerivative": vector(-2.14, -0.07) * mm, "endDerivative": vector(-4.62, 3.18) * mm});
            skFitSpline(sketch, "E197.MirrorCS", {"points": [v(-2.51, 51.81) * mm, v(-4.1, 52.07) * mm, v(-5.07, 52.62) * mm, v(-5.8, 53.12) * mm], "startDerivative": vector(-4.39, 0.34) * mm, "endDerivative": vector(-2.5, 1.65) * mm});
            skArc(sketch, "E198.MirrorCS", {"start": v(-6.38, 46.32) * mm, "mid": v(-8.46, 44.22) * mm, "end": v(-5.8, 45.5) * mm});
            skArc(sketch, "E199.MirrorCS", {"start": v(-6.38, 52.3) * mm, "mid": v(-8.46, 54.4) * mm, "end": v(-5.8, 53.12) * mm});
            skArc(sketch, "E200.MirrorCS", {"start": v(6.4, 52.3) * mm, "mid": v(8.49, 54.4) * mm, "end": v(5.82, 53.12) * mm});
            skArc(sketch, "E201.MirrorCS", {"start": v(6.4, 46.32) * mm, "mid": v(8.49, 44.22) * mm, "end": v(5.82, 45.5) * mm});
            skPoint(sketch, "E202.MirrorP", {"position": v(-8.42, 53.72) * mm});
            skPoint(sketch, "E203.MirrorP", {"position": v(-6.73, 44.6) * mm});
            skPoint(sketch, "E204.MirrorP", {"position": v(-7.49, 43.61) * mm});
            skPoint(sketch, "E205.MirrorP", {"position": v(7.51, 55.01) * mm});
            skPoint(sketch, "E206.MirrorP", {"position": v(6.76, 44.6) * mm});
            skPoint(sketch, "E207.MirrorP", {"position": v(-8.42, 44.9) * mm});
            skPoint(sketch, "E208.MirrorP", {"position": v(8.44, 44.9) * mm});
            skPoint(sketch, "E209.MirrorP", {"position": v(6.76, 54.03) * mm});
            skPoint(sketch, "E210.MirrorP", {"position": v(-7.49, 55.01) * mm});
            skPoint(sketch, "E211.MirrorP", {"position": v(-6.73, 54.03) * mm});
            skPoint(sketch, "E212.MirrorP", {"position": v(7.51, 43.61) * mm});
            skPoint(sketch, "E213.MirrorP", {"position": v(8.44, 53.72) * mm});
            skLineSegment(sketch, "E214.MirrorCS", {"start": v(12.46, 58.36) * mm, "end": v(12.46, 40.36) * mm});
            skLineSegment(sketch, "E215.MirrorCS", {"start": v(-12.54, 58.36) * mm, "end": v(12.46, 58.36) * mm});
            skLineSegment(sketch, "E216.MirrorCS", {"start": v(-12.54, 58.36) * mm, "end": v(-12.54, 40.36) * mm});
            skLineSegment(sketch, "E217.MirrorCS", {"start": v(-12.54, 40.36) * mm, "end": v(12.46, 40.36) * mm});
            skArc(sketch, "E218.MirrorCS", {"start": v(-29.81, 26.94) * mm, "mid": v(-29.8, 26.9) * mm, "end": v(-29.8, 26.87) * mm});
            skFitSpline(sketch, "E219.MirrorCS", {"points": [v(-29.8, 26.87) * mm, v(-29.81, 26.8) * mm, v(-30.05, 26.37) * mm], "startDerivative": vector(0, -0.22) * mm, "endDerivative": vector(-0.44, -0.71) * mm});
            skArc(sketch, "E220.MirrorCS", {"start": v(-29.81, 26.8) * mm, "mid": v(-29.8, 26.83) * mm, "end": v(-29.8, 26.87) * mm});
            skArc(sketch, "E221.MirrorCS", {"start": v(-27.29, 26.8) * mm, "mid": v(-27.3, 26.83) * mm, "end": v(-27.3, 26.87) * mm});
            skFitSpline(sketch, "E222.MirrorCS", {"points": [v(-29.8, 26.87) * mm, v(-29.81, 26.94) * mm, v(-30.05, 27.37) * mm], "startDerivative": vector(0, 0.22) * mm, "endDerivative": vector(-0.44, 0.71) * mm});
            skArc(sketch, "E223.MirrorCS", {"start": v(-27.29, 26.94) * mm, "mid": v(-27.3, 26.9) * mm, "end": v(-27.3, 26.87) * mm});
            skFitSpline(sketch, "E224.MirrorCS", {"points": [v(-27.3, 26.87) * mm, v(-27.29, 26.94) * mm, v(-27.05, 27.37) * mm], "startDerivative": vector(0, 0.22) * mm, "endDerivative": vector(0.44, 0.71) * mm});
            skFitSpline(sketch, "E225.MirrorCS", {"points": [v(-27.3, 26.87) * mm, v(-27.29, 26.8) * mm, v(-27.05, 26.37) * mm], "startDerivative": vector(0, -0.22) * mm, "endDerivative": vector(0.44, -0.71) * mm});
            skFitSpline(sketch, "E226.MirrorCS", {"points": [v(-29.03, 23.12) * mm, v(-29.05, 23.32) * mm, v(-29.23, 23.56) * mm], "startDerivative": vector(0, 0.47) * mm, "endDerivative": vector(-0.58, 0.57) * mm});
            skFitSpline(sketch, "E227.MirrorCS", {"points": [v(-29.23, 23.56) * mm, v(-29.5, 23.75) * mm, v(-29.87, 24.01) * mm, v(-30.05, 24.37) * mm], "startDerivative": vector(-0.53, 0.49) * mm, "endDerivative": vector(-0.1, 0.95) * mm});
            skLineSegment(sketch, "E228.MirrorCS", {"start": v(-28.07, 22.74) * mm, "end": v(-28.07, 23.12) * mm});
            skFitSpline(sketch, "E229.MirrorCS", {"points": [v(-29.23, 30.17) * mm, v(-29.5, 29.98) * mm, v(-29.87, 29.72) * mm, v(-30.05, 29.37) * mm], "startDerivative": vector(-0.53, -0.49) * mm, "endDerivative": vector(-0.1, -0.95) * mm});
            skFitSpline(sketch, "E230.MirrorCS", {"points": [v(-27.87, 23.56) * mm, v(-27.6, 23.75) * mm, v(-27.23, 24.01) * mm, v(-27.05, 24.37) * mm], "startDerivative": vector(0.53, 0.49) * mm, "endDerivative": vector(0.1, 0.95) * mm});
            skFitSpline(sketch, "E231.MirrorCS", {"points": [v(-27.87, 30.17) * mm, v(-27.6, 29.98) * mm, v(-27.23, 29.72) * mm, v(-27.05, 29.37) * mm], "startDerivative": vector(0.53, -0.49) * mm, "endDerivative": vector(0.1, -0.95) * mm});
            skFitSpline(sketch, "E232.MirrorCS", {"points": [v(-28.07, 30.62) * mm, v(-28.05, 30.42) * mm, v(-27.87, 30.17) * mm], "startDerivative": vector(0, -0.47) * mm, "endDerivative": vector(0.58, -0.57) * mm});
            skFitSpline(sketch, "E233.MirrorCS", {"points": [v(-28.07, 23.12) * mm, v(-28.05, 23.32) * mm, v(-27.87, 23.56) * mm], "startDerivative": vector(0, 0.47) * mm, "endDerivative": vector(0.58, 0.57) * mm});
            skFitSpline(sketch, "E234.MirrorCS", {"points": [v(-29.03, 30.62) * mm, v(-29.05, 30.42) * mm, v(-29.23, 30.17) * mm], "startDerivative": vector(0, -0.47) * mm, "endDerivative": vector(-0.58, -0.57) * mm});
            skLineSegment(sketch, "E235.MirrorCS", {"start": v(-29.03, 22.74) * mm, "end": v(-29.03, 23.12) * mm});
            skLineSegment(sketch, "E236.MirrorCS", {"start": v(-28.07, 31) * mm, "end": v(-28.07, 30.62) * mm});
            skLineSegment(sketch, "E237.MirrorCS", {"start": v(-29.03, 31) * mm, "end": v(-29.03, 30.62) * mm});
            skArc(sketch, "E238.MirrorCS", {"start": v(-28.55, 20.87) * mm, "mid": v(-27.58, 21.62) * mm, "end": v(-28.07, 22.74) * mm});
            skFitSpline(sketch, "E239.MirrorCS", {"points": [v(-31.05, 24.34) * mm, v(-31.3, 22.74) * mm, v(-31.86, 21.79) * mm, v(-32.36, 21.06) * mm], "startDerivative": vector(-0.34, -4.39) * mm, "endDerivative": vector(-1.65, -2.5) * mm});
            skArc(sketch, "E240.MirrorCS", {"start": v(-28.55, 32.87) * mm, "mid": v(-29.52, 32.12) * mm, "end": v(-29.03, 31) * mm});
            skFitSpline(sketch, "E241.MirrorCS", {"points": [v(-26.05, 24.34) * mm, v(-25.8, 22.74) * mm, v(-25.24, 21.79) * mm, v(-24.74, 21.06) * mm], "startDerivative": vector(0.34, -4.39) * mm, "endDerivative": vector(1.65, -2.5) * mm});
            skFitSpline(sketch, "E242.MirrorCS", {"points": [v(-26.05, 29.4) * mm, v(-25.8, 30.99) * mm, v(-25.24, 31.95) * mm, v(-24.74, 32.68) * mm], "startDerivative": vector(0.34, 4.39) * mm, "endDerivative": vector(1.65, 2.5) * mm});
            skLineSegment(sketch, "E243.MirrorCS", {"start": v(-37.55, 39.36) * mm, "end": v(-37.55, 14.36) * mm});
            skFitSpline(sketch, "E244.MirrorCS", {"points": [v(-31.05, 29.4) * mm, v(-31.3, 30.99) * mm, v(-31.86, 31.95) * mm, v(-32.36, 32.68) * mm], "startDerivative": vector(-0.34, 4.39) * mm, "endDerivative": vector(-1.65, 2.5) * mm});
            skPoint(sketch, "E245.MirrorP", {"position": v(-22.85, 19.37) * mm});
            skFitSpline(sketch, "E246.MirrorCS", {"points": [v(-27.05, 29.37) * mm, v(-27.05, 29.87) * mm, v(-26.8, 31.16) * mm, v(-25.56, 33.26) * mm], "startDerivative": vector(-0.07, 2.14) * mm, "endDerivative": vector(3.18, 4.62) * mm});
            skLineSegment(sketch, "E247.MirrorCS", {"start": v(-37.55, 14.36) * mm, "end": v(-37.55, 39.36) * mm});
            skArc(sketch, "E248.MirrorCS", {"start": v(-31.54, 20.48) * mm, "mid": v(-33.64, 18.4) * mm, "end": v(-32.36, 21.06) * mm});
            skPoint(sketch, "E249.MirrorP", {"position": v(-24.15, 35.3) * mm});
            skLineSegment(sketch, "E250.MirrorCS", {"start": v(-26.05, 26.87) * mm, "end": v(-26.05, 24.34) * mm});
            skArc(sketch, "E251.MirrorCS", {"start": v(-25.56, 20.48) * mm, "mid": v(-23.46, 18.4) * mm, "end": v(-24.74, 21.06) * mm});
            skLineSegment(sketch, "E252.MirrorCS", {"start": v(-19.55, 14.36) * mm, "end": v(-19.55, 39.36) * mm});
            skLineSegment(sketch, "E253.MirrorCS", {"start": v(-26.05, 26.87) * mm, "end": v(-26.05, 29.4) * mm});
            skLineSegment(sketch, "E254.MirrorCS", {"start": v(-27.05, 26.87) * mm, "end": v(-27.05, 29.37) * mm});
            skLineSegment(sketch, "E255.MirrorCS", {"start": v(-27.05, 26.87) * mm, "end": v(-27.05, 24.37) * mm});
            skPoint(sketch, "E256.MirrorP", {"position": v(-22.85, 34.37) * mm});
            skArc(sketch, "E257.MirrorCS", {"start": v(-28.55, 20.87) * mm, "mid": v(-29.52, 21.62) * mm, "end": v(-29.03, 22.74) * mm});
            skLineSegment(sketch, "E258.MirrorCS", {"start": v(-19.55, 39.36) * mm, "end": v(-37.55, 39.36) * mm});
            skArc(sketch, "E259.MirrorCS", {"start": v(-25.56, 33.26) * mm, "mid": v(-23.46, 35.34) * mm, "end": v(-24.74, 32.68) * mm});
            skPoint(sketch, "E260.MirrorP", {"position": v(-23.83, 33.6) * mm});
            skCircle(sketch, "E261.MirrorC", {"center": v(-28.55, 31.87) * mm, "radius": 1 * mm});
            skPoint(sketch, "E262.MirrorP", {"position": v(-32.95, 35.3) * mm});
            skLineSegment(sketch, "E263.MirrorCS", {"start": v(-19.55, 14.36) * mm, "end": v(-37.55, 14.36) * mm});
            skFitSpline(sketch, "E264.MirrorCS", {"points": [v(-30.05, 24.37) * mm, v(-30.05, 23.87) * mm, v(-30.3, 22.58) * mm, v(-31.54, 20.48) * mm], "startDerivative": vector(0.07, -2.14) * mm, "endDerivative": vector(-3.18, -4.62) * mm});
            skPoint(sketch, "E265.MirrorP", {"position": v(-34.25, 19.37) * mm});
            skFitSpline(sketch, "E266.MirrorCS", {"points": [v(-27.05, 24.37) * mm, v(-27.05, 23.87) * mm, v(-26.8, 22.58) * mm, v(-25.56, 20.48) * mm], "startDerivative": vector(-0.07, -2.14) * mm, "endDerivative": vector(3.18, -4.62) * mm});
            skPoint(sketch, "E267.MirrorP", {"position": v(-32.95, 18.44) * mm});
            skPoint(sketch, "E268.MirrorP", {"position": v(-34.25, 34.37) * mm});
            skLineSegment(sketch, "E269.MirrorCS", {"start": v(-31.05, 26.87) * mm, "end": v(-31.05, 29.4) * mm});
            skLineSegment(sketch, "E270.MirrorCS", {"start": v(-31.05, 26.87) * mm, "end": v(-31.05, 24.34) * mm});
            skArc(sketch, "E271.MirrorCS", {"start": v(-28.55, 32.87) * mm, "mid": v(-27.58, 32.12) * mm, "end": v(-28.07, 31) * mm});
            skCircle(sketch, "E272.MirrorC", {"center": v(-28.55, 21.87) * mm, "radius": 1 * mm});
            skPoint(sketch, "E273.MirrorP", {"position": v(-24.15, 18.44) * mm});
            skPoint(sketch, "E274.MirrorP", {"position": v(-33.27, 33.6) * mm});
            skArc(sketch, "E275.MirrorCS", {"start": v(-31.54, 33.26) * mm, "mid": v(-33.64, 35.34) * mm, "end": v(-32.36, 32.68) * mm});
            skPoint(sketch, "E276.MirrorP", {"position": v(-33.27, 20.12) * mm});
            skFitSpline(sketch, "E277.MirrorCS", {"points": [v(-30.05, 29.37) * mm, v(-30.05, 29.87) * mm, v(-30.3, 31.16) * mm, v(-31.54, 33.26) * mm], "startDerivative": vector(0.07, 2.14) * mm, "endDerivative": vector(-3.18, 4.62) * mm});
            skLineSegment(sketch, "E278.MirrorCS", {"start": v(-30.05, 26.87) * mm, "end": v(-30.05, 24.37) * mm});
            skPoint(sketch, "E279.MirrorP", {"position": v(-23.83, 20.12) * mm});
            skLineSegment(sketch, "E280.MirrorCS", {"start": v(-30.05, 26.87) * mm, "end": v(-30.05, 29.37) * mm});
            skSolve(sketch);
        }
        {
            var Q0;
            Q0=makeQuery(id+"F0.imprint","IMPRINT",FACE,{"disambiguationData":[TD([[makeQuery(id+"F0.imprint","IMPRINT",EDGE,{"derivedFrom":sQuery(id+"F0.wireOp",EDGE,"E24.MirrorCS")}),-1.0]])]});
            extrude(context, id + "F1", {"entities" : qUnion([Q0]), "depth" : 1.5 * mm});
        }
        {
            var Q0;
            Q0=makeQuery(id+"F0.imprint","IMPRINT",FACE,{"disambiguationData":[TD([[makeQuery(id+"F0.imprint","IMPRINT",EDGE,{"derivedFrom":sQuery(id+"F0.wireOp",EDGE,"E11")}),-1.0]])]});
            extrude(context, id + "F2", {"entities" : qUnion([Q0]), "depth" : 1.5 * mm});
        }
        {
            var Q0;
            {var subQ10=sQuery(id+"F0.wireOp",EDGE,"E8");Q0=makeQuery(id+"F0.imprint","IMPRINT",FACE,{"disambiguationData":[TD([[makeQuery(id+"F0.imprint","IMPRINT",EDGE,{"derivedFrom":subQ10}),1.0]])]});}
            var Q1;
            {var subQ0=sQuery(id+"F0.wireOp",EDGE,"E49.MirrorC");var subQ1=makeQuery(id+"F0.imprint","INTERSECT",VERTEX,{"derivedFrom":[sQuery(id+"F0.wireOp",EDGE,"E36.MirrorCS"),subQ0]});Q1=makeQuery(id+"F0.imprint","IMPRINT",FACE,{"disambiguationData":[TD([[makeQuery(id+"F0.imprint","IMPRINT",EDGE,{"disambiguationData":[TD([[subQ1,-1.0]])],"derivedFrom":subQ0}),-1.0]])]});}
            var Q2;
            {var subQ0=sQuery(id+"F0.wireOp",EDGE,"E31");var subQ1=makeQuery(id+"F0.imprint","INTERSECT",VERTEX,{"derivedFrom":[sQuery(id+"F0.wireOp",EDGE,"E8"),subQ0]});Q2=makeQuery(id+"F0.imprint","IMPRINT",FACE,{"disambiguationData":[TD([[makeQuery(id+"F0.imprint","IMPRINT",EDGE,{"disambiguationData":[TD([[subQ1,-1.0]])],"derivedFrom":subQ0}),1.0]])]});}
            extrude(context, id + "F3", {"entities" : qUnion([Q0, Q1, Q2]), "depth" : 1 * mm});
        }
    });
